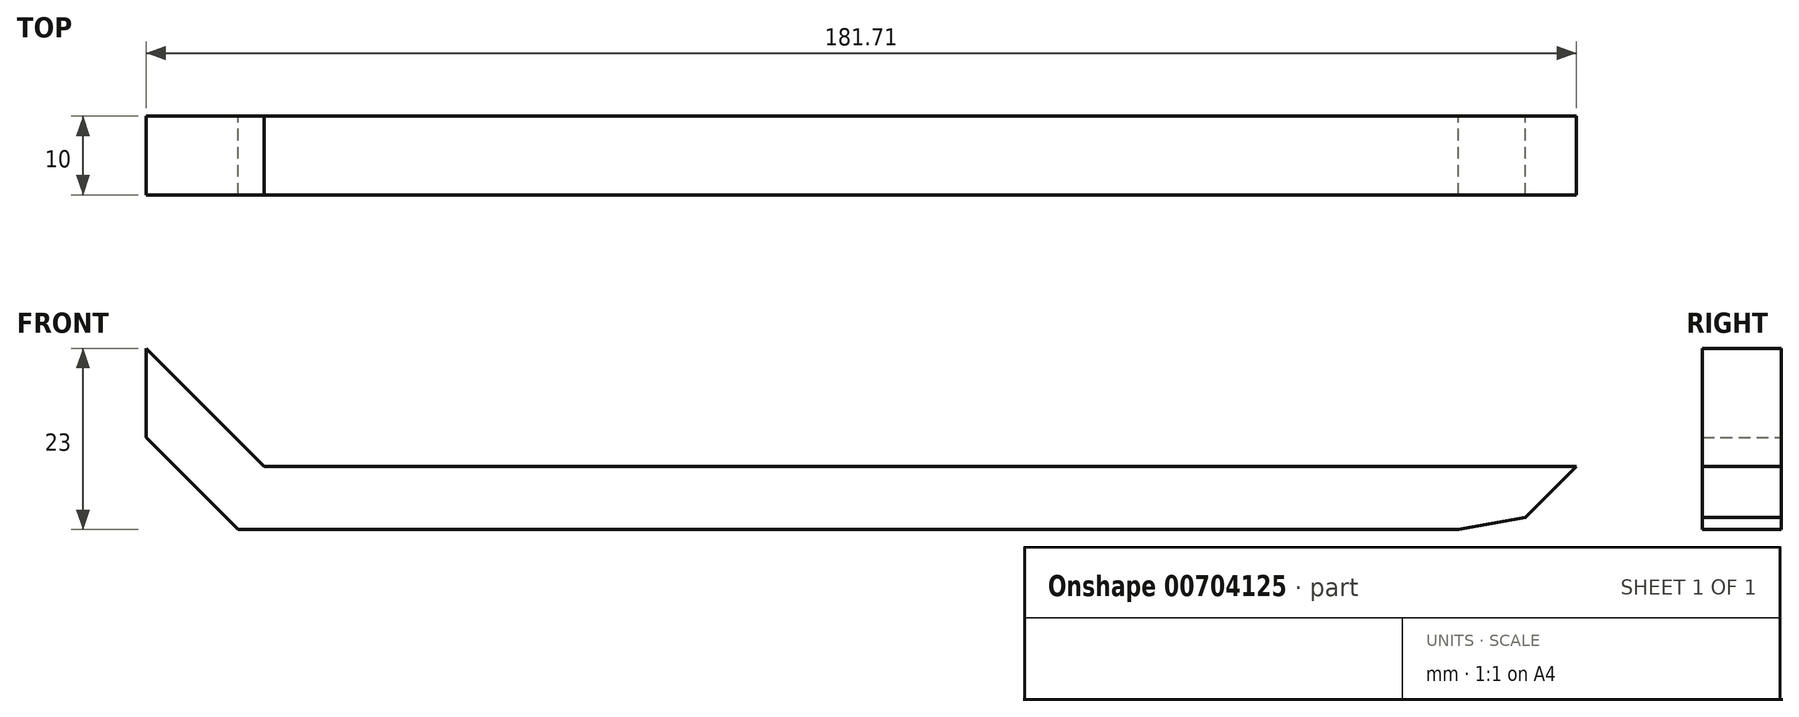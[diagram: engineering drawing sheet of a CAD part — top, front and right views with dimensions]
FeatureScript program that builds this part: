
annotation { "Feature Type Name" : "Feature", "Feature Type Description" : "" }
export const myFeature = defineFeature(function(context is Context, id is Id, definition is map)
    precondition{}
    {
        {
            var Q0;
            Q0=qCreatedBy(makeId("Front.planeOp"),FACE);
            var sketch = newSketch(context, id + "F0", { "sketchPlane" : qUnion([Q0])});
            skLineSegment(sketch, "E0", {"start": v(170.02, 8) * mm, "end": v(163.52, 1.5) * mm});
            skLineSegment(sketch, "E1", {"start": v(163.52, 1.5) * mm, "end": v(155.02, 0) * mm});
            skLineSegment(sketch, "E2", {"start": v(-11.69, 23) * mm, "end": v(-11.69, 11.69) * mm});
            skLineSegment(sketch, "E3", {"start": v(-11.69, 11.69) * mm, "end": v(0, 0) * mm});
            skLineSegment(sketch, "E4", {"start": v(3.31, 8) * mm, "end": v(-11.69, 23) * mm});
            skLineSegment(sketch, "E5", {"start": v(3.31, 8) * mm, "end": v(170.02, 8) * mm});
            skLineSegment(sketch, "E6", {"start": v(0, 0) * mm, "end": v(155.02, 0) * mm});
            skSolve(sketch);
        }
        {
            var Q0;
            Q0=qSketchRegion(id+"F0",true);
            extrude(context, id + "F1", {"entities" : qUnion([Q0]), "depth" : 10 * mm, "offsetDistance" : 25 * mm});
        }
    });
